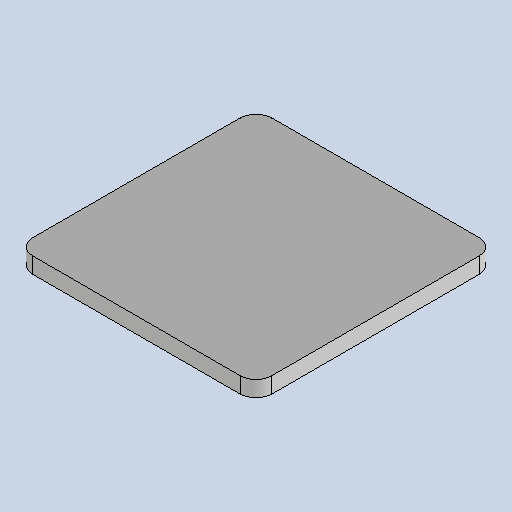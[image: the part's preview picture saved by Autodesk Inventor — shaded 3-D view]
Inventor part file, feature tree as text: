
AUTODESK INVENTOR PART (.ipt)
format: ipt  version: 2025.1 (Build 291241020, 241B)  size: 143,360 bytes
history: native  units: mm
features: other x2, sheet_metal_op x1, chamfer x1, sketch x1
ambient origin geometry x8: Origin, YZ Plane, XZ Plane, XY Plane, X Axis, Y Axis, Z Axis, Center Point
bodies: Body1 (feature_tree)
feature tree (5):
  sheet_metal_op  "Face3"
  chamfer  "Corner Round1"
  sketch  "Sketch1"  dims[d154=30.0mm d155=30.0mm d156=2.0mm d178=2.0mm]
  other  "Plate5"
  other  "Definition1"
